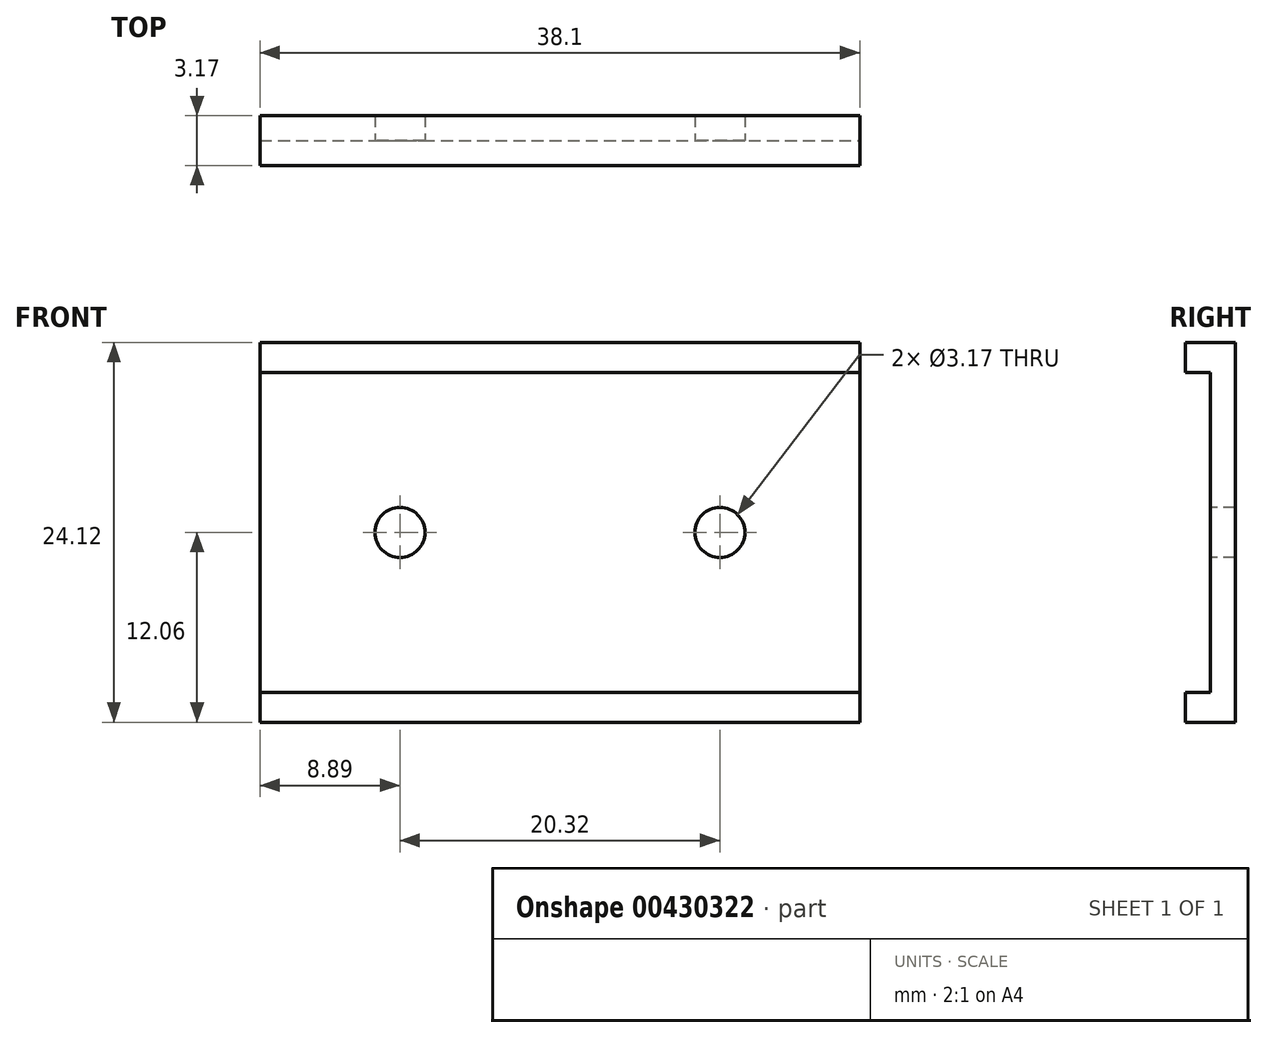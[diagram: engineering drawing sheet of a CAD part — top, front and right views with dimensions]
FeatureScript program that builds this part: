
annotation { "Feature Type Name" : "Feature", "Feature Type Description" : "" }
export const myFeature = defineFeature(function(context is Context, id is Id, definition is map)
    precondition{}
    {
        {
            var Q0;
            Q0=qCreatedBy(makeId("Front.planeOp"),FACE);
            var sketch = newSketch(context, id + "F0", { "sketchPlane" : qUnion([Q0])});
            skLineSegment(sketch, "E0.bottom", {"start": v(19.05, 9.53) * mm, "end": v(-19.05, 9.53) * mm});
            skLineSegment(sketch, "E0.top", {"start": v(19.05, -9.53) * mm, "end": v(-19.05, -9.53) * mm});
            skLineSegment(sketch, "E0.left", {"start": v(19.05, 9.53) * mm, "end": v(19.05, -9.53) * mm});
            skLineSegment(sketch, "E0.right", {"start": v(-19.05, 9.53) * mm, "end": v(-19.05, -9.53) * mm});
            skPoint(sketch, "E0.middle", {"position": v(0, 0) * mm});
            skSolve(sketch);
        }
        {
            var Q0;
            Q0=makeQuery(id+"F0.imprint","IMPRINT",FACE,{"disambiguationData":[TD([[makeQuery(id+"F0.imprint","IMPRINT",EDGE,{"derivedFrom":sQuery(id+"F0.wireOp",EDGE,"E0.bottom")}),1.0]])]});
            extrude(context, id + "F1", {"entities" : qUnion([Q0]), "depth" : 1.59 * mm});
        }
        {
            var Q0;
            Q0=makeQuery(id+"F1.opExtrude","CAP_FACE",FACE,{"disambiguationData":[OSD([sQuery(id+"F0.wireOp",EDGE,"E0.bottom"),sQuery(id+"F0.wireOp",EDGE,"E0.top"),sQuery(id+"F0.wireOp",EDGE,"E0.left"),sQuery(id+"F0.wireOp",EDGE,"E0.right")])],"isStart":false});
            var sketch = newSketch(context, id + "F2", { "sketchPlane" : qUnion([Q0])});
            skPoint(sketch, "E1", {"position": v(-10.16, 0) * mm});
            skPoint(sketch, "E1.positionSnap0", {"position": v(-19.05, 0) * mm});
            skPoint(sketch, "E2", {"position": v(10.16, 0) * mm});
            skCircle(sketch, "E3", {"center": v(-10.16, 0) * mm, "radius": 1.59 * mm});
            skCircle(sketch, "E4", {"center": v(10.16, 0) * mm, "radius": 1.59 * mm});
            skSolve(sketch);
        }
        {
            var Q0;
            Q0=makeQuery(id+"F2.imprint","IMPRINT",FACE,{"disambiguationData":[TD([[makeQuery(id+"F2.imprint","IMPRINT",EDGE,{"derivedFrom":sQuery(id+"F2.wireOp",EDGE,"E3")}),1.0]])]});
            var Q1;
            Q1=makeQuery(id+"F2.imprint","IMPRINT",FACE,{"disambiguationData":[TD([[makeQuery(id+"F2.imprint","IMPRINT",EDGE,{"derivedFrom":sQuery(id+"F2.wireOp",EDGE,"E4")}),1.0]])]});
            extrude(context, id + "F3", {"entities" : qUnion([Q0, Q1]), "operationType" : NewBodyOperationType.REMOVE, "endBound" : BoundingType.THROUGH_ALL, "oppositeDirection" : true, "depth" : 25.4 * mm});
        }
        {
            var Q0;
            Q0=makeQuery(id+"F1.opExtrude","CAP_FACE",FACE,{"disambiguationData":[OSD([sQuery(id+"F0.wireOp",EDGE,"E0.bottom"),sQuery(id+"F0.wireOp",EDGE,"E0.top"),sQuery(id+"F0.wireOp",EDGE,"E0.left"),sQuery(id+"F0.wireOp",EDGE,"E0.right")])],"isStart":false});
            var sketch = newSketch(context, id + "F4", { "sketchPlane" : qUnion([Q0])});
            skLineSegment(sketch, "E5.bottom", {"start": v(-19.05, -9.53) * mm, "end": v(19.05, -9.53) * mm});
            skLineSegment(sketch, "E5.top", {"start": v(-19.05, -12.06) * mm, "end": v(19.05, -12.06) * mm});
            skLineSegment(sketch, "E5.left", {"start": v(-19.05, -9.53) * mm, "end": v(-19.05, -12.06) * mm});
            skLineSegment(sketch, "E5.right", {"start": v(19.05, -9.53) * mm, "end": v(19.05, -12.06) * mm});
            skLineSegment(sketch, "E6.bottom", {"start": v(-19.05, 9.53) * mm, "end": v(19.05, 9.53) * mm});
            skLineSegment(sketch, "E6.top", {"start": v(-19.05, 12.07) * mm, "end": v(19.05, 12.07) * mm});
            skLineSegment(sketch, "E6.left", {"start": v(-19.05, 9.53) * mm, "end": v(-19.05, 12.06) * mm});
            skLineSegment(sketch, "E6.right", {"start": v(19.05, 9.53) * mm, "end": v(19.05, 12.07) * mm});
            skSolve(sketch);
        }
        {
            var Q0;
            Q0=makeQuery(id+"F4.imprint","IMPRINT",FACE,{"disambiguationData":[TD([[makeQuery(id+"F4.imprint","IMPRINT",EDGE,{"derivedFrom":sQuery(id+"F4.wireOp",EDGE,"E5.bottom")}),1.0]])]});
            var Q1;
            Q1=makeQuery(id+"F4.imprint","IMPRINT",FACE,{"disambiguationData":[TD([[makeQuery(id+"F4.imprint","IMPRINT",EDGE,{"derivedFrom":sQuery(id+"F4.wireOp",EDGE,"E6.bottom")}),-1.0]])]});
            extrude(context, id + "F5", {"entities" : qUnion([Q0, Q1]), "operationType" : NewBodyOperationType.ADD, "endBound" : BoundingType.SYMMETRIC, "depth" : 3.17 * mm});
        }
        {
            var Q0;
            Q0=makeQuery(id+"F5.opExtrude","CAP_FACE",FACE,{"disambiguationData":[OSD([sQuery(id+"F4.wireOp",EDGE,"E6.bottom"),sQuery(id+"F4.wireOp",EDGE,"E6.top"),sQuery(id+"F4.wireOp",EDGE,"E6.left"),sQuery(id+"F4.wireOp",EDGE,"E6.right")])],"isStart":false});
            var sketch = newSketch(context, id + "F6", { "sketchPlane" : qUnion([Q0])});
            skLineSegment(sketch, "E7.bottom", {"start": v(-19.05, 9.53) * mm, "end": v(19.05, 9.53) * mm});
            skLineSegment(sketch, "E8.top", {"start": v(-19.05, 10.16) * mm, "end": v(19.05, 10.16) * mm});
            skLineSegment(sketch, "E8.left", {"start": v(-19.05, 9.53) * mm, "end": v(-19.05, 10.16) * mm});
            skLineSegment(sketch, "E8.right", {"start": v(19.05, 9.53) * mm, "end": v(19.05, 10.16) * mm});
            skSolve(sketch);
        }
        {
            var Q0;
            Q0=makeQuery(id+"F6.imprint","IMPRINT",FACE,{"disambiguationData":[TD([[makeQuery(id+"F6.imprint","IMPRINT",EDGE,{"derivedFrom":sQuery(id+"F6.wireOp",EDGE,"E7.bottom")}),-1.0]])]});
            extrude(context, id + "F7", {"entities" : qUnion([Q0]), "operationType" : NewBodyOperationType.REMOVE, "oppositeDirection" : true, "depth" : 1.59 * mm});
        }
        {
            var Q0;
            Q0=makeQuery(id+"F5.opExtrude","CAP_FACE",FACE,{"disambiguationData":[OSD([sQuery(id+"F4.wireOp",EDGE,"E5.bottom"),sQuery(id+"F4.wireOp",EDGE,"E5.top"),sQuery(id+"F4.wireOp",EDGE,"E5.left"),sQuery(id+"F4.wireOp",EDGE,"E5.right")])],"isStart":false});
            var sketch = newSketch(context, id + "F8", { "sketchPlane" : qUnion([Q0])});
            skLineSegment(sketch, "E9.bottom", {"start": v(-19.05, -9.53) * mm, "end": v(19.05, -9.53) * mm});
            skLineSegment(sketch, "E10.top", {"start": v(-19.05, -10.16) * mm, "end": v(19.05, -10.16) * mm});
            skLineSegment(sketch, "E10.left", {"start": v(-19.05, -9.53) * mm, "end": v(-19.05, -10.16) * mm});
            skLineSegment(sketch, "E10.right", {"start": v(19.05, -9.53) * mm, "end": v(19.05, -10.16) * mm});
            skSolve(sketch);
        }
        {
            var Q0;
            Q0=makeQuery(id+"F8.imprint","IMPRINT",FACE,{"disambiguationData":[TD([[makeQuery(id+"F8.imprint","IMPRINT",EDGE,{"derivedFrom":sQuery(id+"F8.wireOp",EDGE,"E9.bottom")}),1.0]])]});
            extrude(context, id + "F9", {"entities" : qUnion([Q0]), "operationType" : NewBodyOperationType.REMOVE, "oppositeDirection" : true, "depth" : 1.59 * mm});
        }
    });
